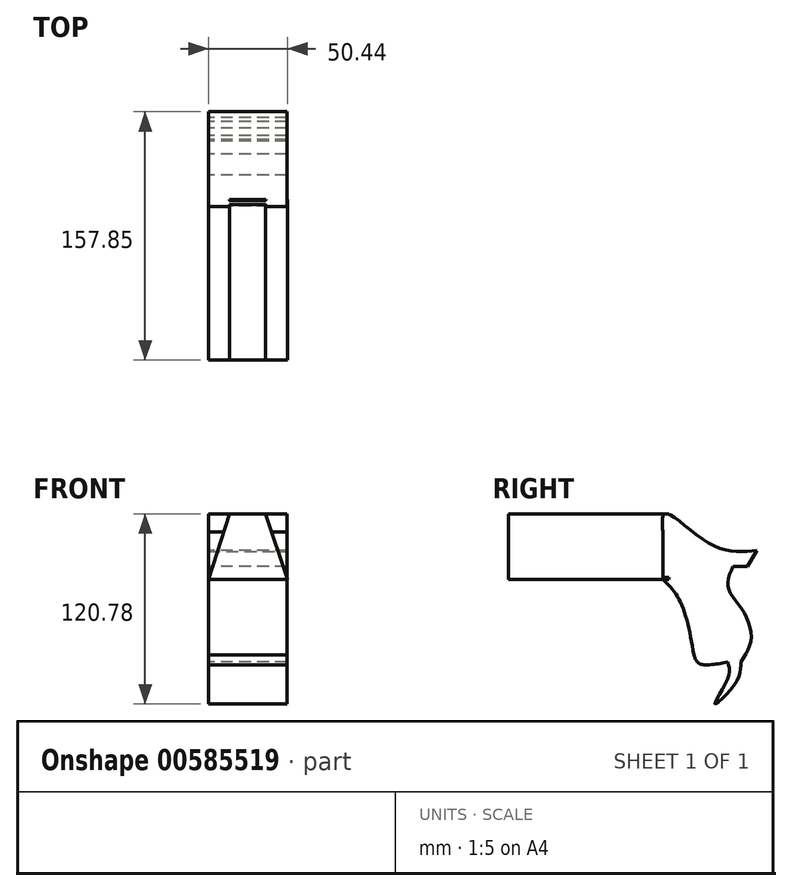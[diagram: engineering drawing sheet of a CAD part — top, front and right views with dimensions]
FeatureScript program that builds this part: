
annotation { "Feature Type Name" : "Feature", "Feature Type Description" : "" }
export const myFeature = defineFeature(function(context is Context, id is Id, definition is map)
    precondition{}
    {
        {
            var Q0;
            Q0=qCreatedBy(makeId("Right.planeOp"),FACE);
            var sketch = newSketch(context, id + "F0", { "sketchPlane" : qUnion([Q0])});
            skFitSpline(sketch, "E0", {"points": [v(97.92, 0) * mm, v(108.66, -13.27) * mm, v(117.75, -47.99) * mm], "startDerivative": vector(28.56, -27.17) * mm, "endDerivative": vector(12.12, -66.4) * mm});
            skFitSpline(sketch, "E1", {"points": [v(117.75, -47.99) * mm, v(121.06, -53.36) * mm, v(139.25, -52.53) * mm], "startDerivative": vector(5.22, -17.43) * mm, "endDerivative": vector(35.18, 6.3) * mm});
            skFitSpline(sketch, "E2", {"points": [v(139.25, -52.53) * mm, v(139.25, -62.87) * mm, v(130.98, -78.99) * mm, v(144.2, -65.76) * mm, v(147.51, -52.53) * mm], "startDerivative": vector(12.36, -41.29) * mm, "endDerivative": vector(-0.25, 50.18) * mm});
            skFitSpline(sketch, "E3", {"points": [v(147.51, -52.53) * mm, v(154.13, -36.83) * mm, v(147.51, -17.82) * mm, v(139.25, -4.6) * mm, v(142.55, 8.22) * mm], "startDerivative": vector(37.18, 58.72) * mm, "endDerivative": vector(27.01, 58.83) * mm});
            skLineSegment(sketch, "E4", {"start": v(142.55, 8.22) * mm, "end": v(151.65, 8.22) * mm});
            skLineSegment(sketch, "E5", {"start": v(97.92, 0) * mm, "end": v(97.92, 30.13) * mm});
            skLineSegment(sketch, "E6", {"start": v(151.65, 8.22) * mm, "end": v(157.85, 18.55) * mm});
            skFitSpline(sketch, "E7", {"points": [v(157.85, 18.55) * mm, v(129.33, 21.86) * mm, v(99.57, 41.7) * mm, v(97.92, 30.13) * mm], "startDerivative": vector(-74.42, -9.29) * mm, "endDerivative": vector(5.76, -71.67) * mm});
            skSolve(sketch);
        }
        {
            var Q0;
            Q0=makeQuery(id+"F0.imprint","IMPRINT",FACE,{"disambiguationData":[TD([[makeQuery(id+"F0.imprint","IMPRINT",EDGE,{"derivedFrom":sQuery(id+"F0.wireOp",EDGE,"E0")}),1.0]])]});
            extrude(context, id + "F1", {"entities" : qUnion([Q0]), "depth" : 25 * mm, "offsetDistance" : 25 * mm, "hasSecondDirection" : true, "secondDirectionOppositeDirection" : true, "secondDirectionDepth" : 25 * mm});
        }
        {
            var Q0;
            Q0=qCreatedBy(makeId("Front.planeOp"),FACE);
            var sketch = newSketch(context, id + "F2", { "sketchPlane" : qUnion([Q0])});
            skLineSegment(sketch, "E8", {"start": v(-25, 0) * mm, "end": v(-11.5, 41.47) * mm});
            skLineSegment(sketch, "E9", {"start": v(-11.5, 41.47) * mm, "end": v(0, 41.47) * mm});
            skLineSegment(sketch, "E10", {"start": v(0, 0) * mm, "end": v(-25, 0) * mm});
            skLineSegment(sketch, "E11", {"start": v(25.44, 0) * mm, "end": v(0, 0) * mm});
            skLineSegment(sketch, "E12", {"start": v(0, 41.47) * mm, "end": v(-11.5, 41.47) * mm});
            skLineSegment(sketch, "E13", {"start": v(0, 41.47) * mm, "end": v(11.44, 41.47) * mm});
            skLineSegment(sketch, "E14", {"start": v(11.44, 41.47) * mm, "end": v(25.44, 0) * mm});
            skSolve(sketch);
        }
        {
            var Q0;
            Q0=makeQuery(id+"F2.imprint","IMPRINT",FACE,{"disambiguationData":[TD([[makeQuery(id+"F2.imprint","IMPRINT",EDGE,{"derivedFrom":sQuery(id+"F2.wireOp",EDGE,"E8")}),-1.0]])]});
            extrude(context, id + "F3", {"entities" : qUnion([Q0]), "operationType" : NewBodyOperationType.ADD, "oppositeDirection" : true, "depth" : 102 * mm, "offsetDistance" : 25 * mm});
        }
    });
